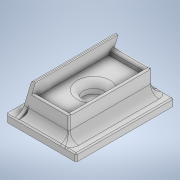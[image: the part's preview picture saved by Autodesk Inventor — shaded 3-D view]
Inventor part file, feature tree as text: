
AUTODESK INVENTOR PART (.ipt)
format: ipt  version: 2021 (Build 250183000, 183)  size: 306,176 bytes
history: native  units: in
note: dims shown in document units (in); Inventor stores cm internally (conversion verified against a paired STEP export)
features: projected_geometry x9, extrude x7, sketch x7, fillet x6, chamfer x2
ambient origin geometry x8: Origin, YZ Plane, XZ Plane, XY Plane, X Axis, Y Axis, Z Axis, Center Point
bodies: Solid1 (feature_tree)
feature tree (31):
  extrude  "Extrusion1"  Depth=2.6575in
  extrude  "Extrusion2"  Depth=0.1181in
  extrude  "Extrusion3"  Depth=0.2362in TaperAngle=0.0deg
  extrude  "Extrusion5"  Depth=0.2362in
  extrude  "Extrusion11"  Depth=0.6693in
  extrude  "Extrusion10"  Depth=0.3543in TaperAngle=0.0deg
  fillet  "Fillet7"  Radius=0.3937in
  fillet  "Fillet8"  Radius=0.3937in
  fillet  "Fillet9"  Radius=0.1181in
  chamfer  "Chamfer2"  [1 undecoded]
  fillet  "Fillet16"  [1 undecoded]
  fillet  "Fillet13"  Radius=0.3543in
  fillet  "Fillet14"  Radius=0.1181in
  chamfer  "Chamfer1"  Distance=0.0394in
  extrude  "Extrusion9"  Depth=0.2756in
  sketch  "Sketch1"  dims[d0=1.2992in d1=2.6575in]
  sketch  "Sketch2"  dims[d2=0.9685in d3=0.0in d4=0.1181in]
  sketch  "Sketch4"  dims[d5=0.1181in d6=0.2362in d7=0.0in]
  sketch  "Sketch6"  dims[d10=0.4724in d11=0.2362in]
  projected_geometry  "Projected Loop1"
  sketch  "Sketch7"  dims[d12=0.2362in d13=0.0in d25=0.6693in]
  projected_geometry  "Projected Loop2"
  sketch  "Sketch10"  dims[d26=0.4134in d27=0.3543in d28=0.0in d29=0.3937in d30=0.3937in d31=0.1181in d38=0.0in d39=0.0in d40=0.0in d41=0.0in d42=0.3543in d43=0.0in d44=0.1181in]
  projected_geometry  "Projected Loop5"
  projected_geometry  "Projected Loop6"
  projected_geometry  "Projected Loop7"
  projected_geometry  "Projected Loop8"
  sketch  "Sketch11"  dims[d45=0.1969in d46=0.0394in d50=0.2756in d51=0.2756in d53=0.0394in d54=0.0787in d55=45.0deg d56=0.0787in d57=0.0787in d58=45.0deg d59=0.0394in]
  projected_geometry  "Projected Loop9"
  projected_geometry  "Projected Loop10"
  projected_geometry  "Projected Loop11"
note: 2 required parameter values undecoded (feature->parameter linkage not recoverable at this tier; creation-order binding heuristic only, values carry confidence <= 0.55)
